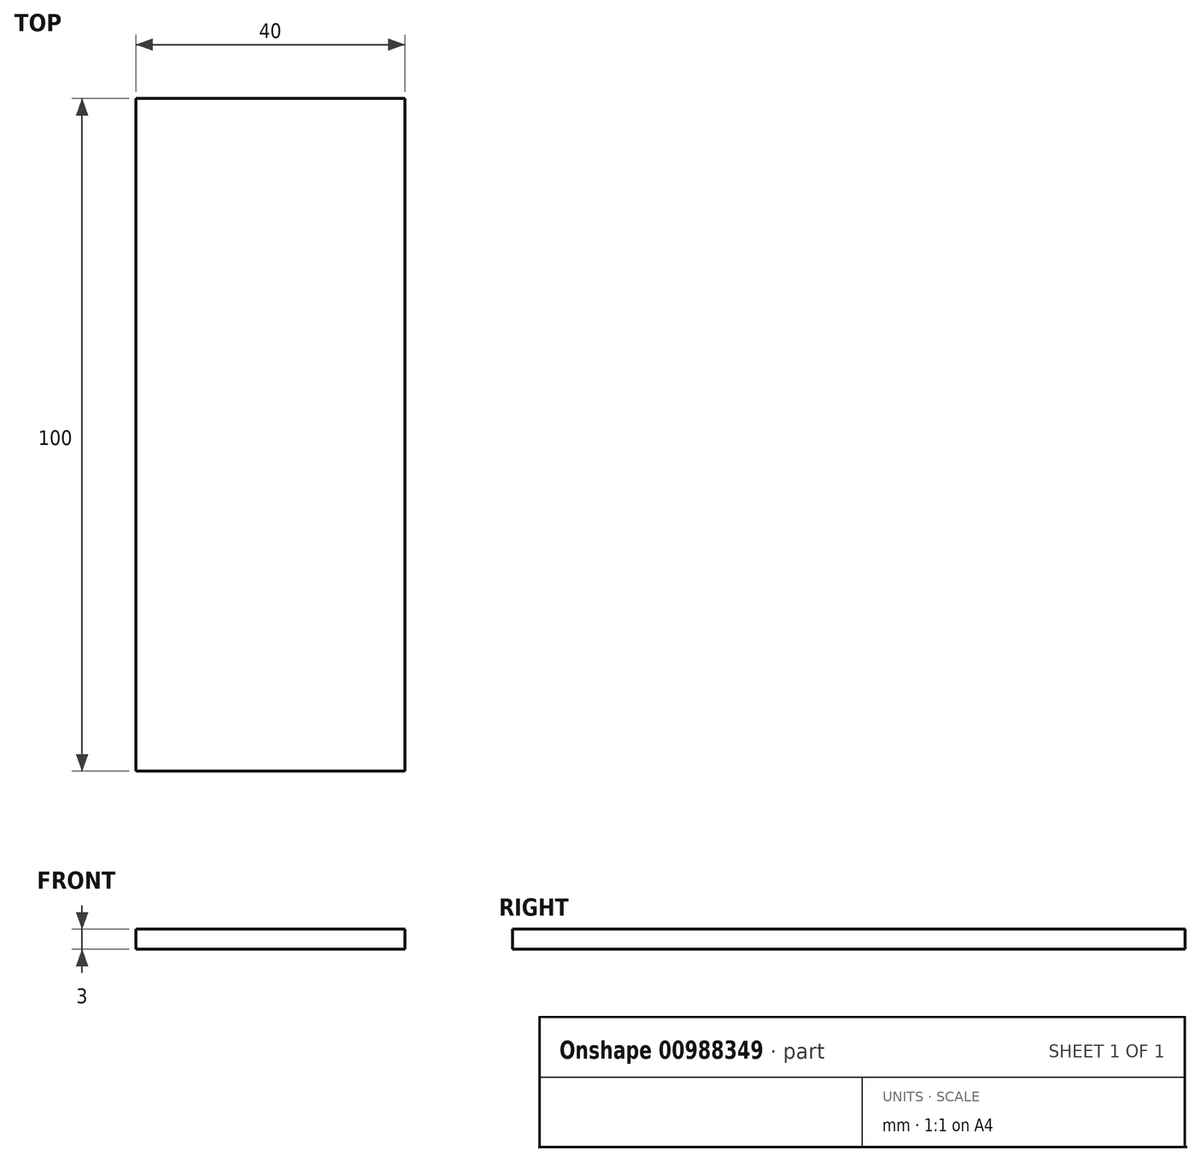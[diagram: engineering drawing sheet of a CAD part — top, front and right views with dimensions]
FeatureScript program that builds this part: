
annotation { "Feature Type Name" : "Feature", "Feature Type Description" : "" }
export const myFeature = defineFeature(function(context is Context, id is Id, definition is map)
    precondition{}
    {
        {
            var Q0;
            Q0=qCreatedBy(makeId("Top.planeOp"),FACE);
            var sketch = newSketch(context, id + "F0", { "sketchPlane" : qUnion([Q0])});
            skLineSegment(sketch, "E0.bottom", {"start": v(40, 0) * mm, "end": v(0, 0) * mm});
            skLineSegment(sketch, "E0.top", {"start": v(40, 100) * mm, "end": v(0, 100) * mm});
            skLineSegment(sketch, "E0.left", {"start": v(40, 0) * mm, "end": v(40, 100) * mm});
            skLineSegment(sketch, "E0.right", {"start": v(0, 0) * mm, "end": v(0, 100) * mm});
            skSolve(sketch);
        }
        {
            var Q0;
            Q0=makeQuery(id+"F0.imprint","IMPRINT",FACE,{"disambiguationData":[TD([[makeQuery(id+"F0.imprint","IMPRINT",EDGE,{"derivedFrom":sQuery(id+"F0.wireOp",EDGE,"E0.bottom")}),-1.0]])]});
            extrude(context, id + "F1", {"entities" : qUnion([Q0]), "depth" : 3 * mm, "offsetDistance" : 25 * mm});
        }
    });
